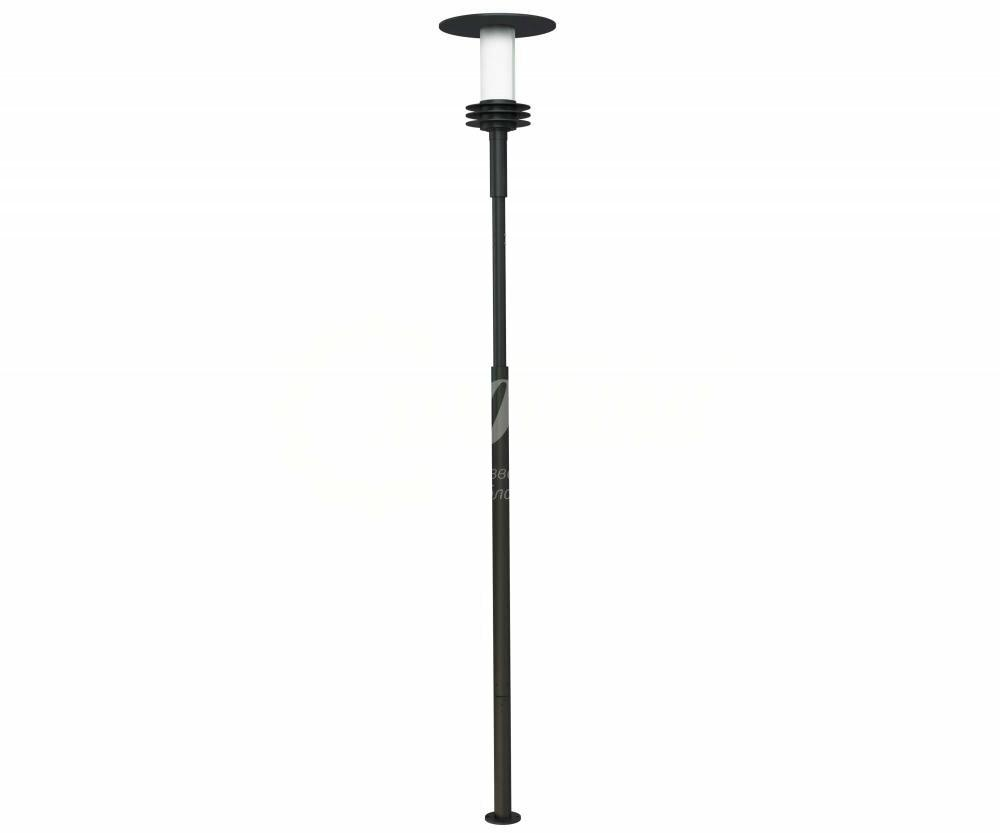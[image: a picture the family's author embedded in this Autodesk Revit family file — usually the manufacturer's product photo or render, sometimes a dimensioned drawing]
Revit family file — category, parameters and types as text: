
# Revit family: 7526 Уличный фонарь «Техно - 1» Хоббика
name_source: partatom
category: Антураж
revit_build: Autodesk Revit 2018 (Build: 20180423_1000(x64)
units: mm (PartAtom-declared; Revit-internal decimal feet)

## family parameters
Всегда вертикально = Да
Источник визуального образа = Геометрия семейства
На основе рабочей плоскости = Нет
Общий = Нет
При загрузке вырезать с полостями = Нет
Точка расчета площади = Нет

## types (4) — shared parameters
URL = https://hobbyka.ru
Артикул товара = Арт. 7526
Группа модели = Светильники со стальными опорами
Изготовитель = ООО «Хоббика»
Изображение типоразмера = Уличный фонарь «Техно - 1» Арт 7526.jpg
Материал изделия = Сталь
Цвет каркаса = Сталь
Ширина = 511 мм

## per-type parameters (varying)
| type | Версия 3,5 м | Версия 4,0 м | Версия 4,5 м | Версия 5,0 м | Высота | Описание |
| Версия 3,5 м | Да | Нет | Нет | Нет | 3500 мм | Уличный фонарь «Техно - 1». Версия 3,5 м |
| Версия 4,0 м | Нет | Да | Нет | Нет | 4000 мм | Уличный фонарь «Техно - 1». Версия 4,0 м |
| Версия 4,5 м | Нет | Нет | Да | Нет | 4500 мм | Уличный фонарь «Техно - 1». Версия 4,5 м |
| Версия 5,0 м | Нет | Нет | Нет | Да | 5000 мм | Уличный фонарь «Техно - 1». Версия 5,0 м |
